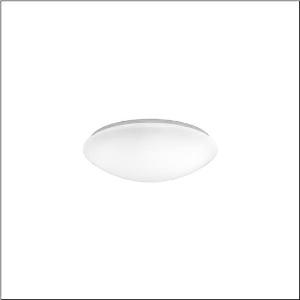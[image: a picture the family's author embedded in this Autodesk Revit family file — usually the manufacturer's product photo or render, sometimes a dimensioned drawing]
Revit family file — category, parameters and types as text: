
# Revit family: round_31_b_5pja012001a
name_source: partatom
category: Lighting Fixtures
units: mm (PartAtom-declared; Revit-internal decimal feet)

## family parameters
Cut with Voids When Loaded = No
Host = Face
Light Source = No
Part Type = Normal
Room Calculation Point = No
Round Connector Dimension = Use Diameter
Shared = No

## types (1)
- Round 31 B (1 x LED, 1800 lm, 15 W, 3000K)
    Apparent Load = 15 VA
    CIE Flux Codes = 42 71 89 88 100
    Color Rendering = 80
    Color Temperature = 3000K
    Default Elevation = 1800 mm  [stored 5.90551 ft]
    Description = Round 31 B, wall and ceiling luminaire, primary optical cover: enclosure, of PMMA, light emission: direct distribution, primary light characteristic: symmetric, installation type: surface-mounted, LED, rated luminous flux: 1.800lm, luminous efficacy: 120lm/W, light colour: 830, colour temperature: 3000K, with terminal, 3+2-pole, max. 2.5mm², mains connection: 230V, AC, 50/60Hz, rated input power: 15W, luminaire housing, round, of steel, white, diameter: 290mm, height: 85mm, protection rating (complete): IP40, insulation class (complete): insulation class I (protective earthing), certification: CE, impact resistance: IK02, permissible operating ambient temperature: -20..+25°C, packaging unit: 1 piece
    Height = 85 mm
    Lamp = 1 x LED
    Lamp Light Flux = 1800 lm
    Lamp Power = 15 W
    Lamp count = 1
    Length = 290 mm
    Luminous efficacy = 120 lm/W
    Manufacturer = Siteco
    ModVariant = No
    Model = 5PJA012001A
    Mounting Place = Ceiling
    Mounting Type = Surface mounted
    Number of Poles = 1
    OnlyDefault = Yes
    Power Factor = 1
    Product Name = Round 31 B
    Product group = wall and ceiling luminaire
    ProductGroupID = 302
    Protection Class = Protection class I
    Protection Degree = IP 40
    RLX_Detail_Level = 1
    RLX_Emergency_Light_Flux = 0 lm
    RLX_Emergency_Type = 0
    RLX_Emergency_Type_DB = No
    RlxData = <blob elided: 9241 chars, md5=8de99cd4>
    Socket = socket
    Standby Power = 0 W
    System Light Flux = 1800 lm
    System Power = 15 W
    Type Comments = Product without accessories
    Type Image = l_1258346.jpg
    URL = http://relux.com
    VarID = ---
    Voltage = 0 V
    Weight = 0.00 kg
    Width = 0 mm  [stored 0 ft]

note: [stored X ft] marks values corroborated as IEEE doubles in the binary element streams (Revit-internal decimal feet)

## geometry (parser evidence)
native form markers: Sweep x11
no freeform markers — native parametric forms only
